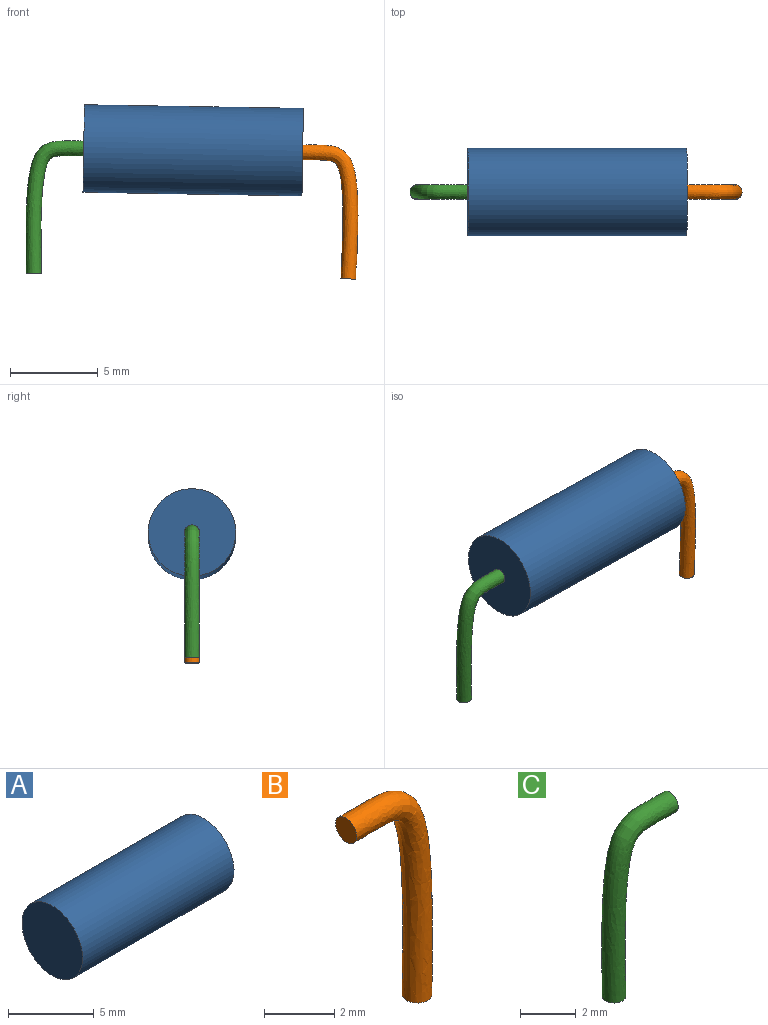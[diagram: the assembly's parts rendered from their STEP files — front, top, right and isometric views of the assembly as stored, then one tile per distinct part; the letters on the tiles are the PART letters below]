
ASSEMBLY  parts=3 mates=2
PART A: 3 faces, bbox 12.5x5x5 mm
  f0: cylinder r=2.5mm len=12.5mm, axis (-1,0,0), area 196.3mm2, adj f1,f2
  f1: plane 5x5mm, normal (1,0,0), area 19.6mm2, adj f0
  f2: plane 5x5mm, normal (-1,0,0), area 19.6mm2, adj f0
PART B: 3 faces, bbox 3.3x1.7x7.6 mm
  f0: plane 0.85x0.85mm, normal (-0.02,0,-1), area 0.6mm2, adj f2
  f1: plane 0.85x0.85mm, normal (-1,0,-0.02), area 0.6mm2, adj f2
  f2: bspline ~7.59x3.33mm, area 24.7mm2, adj f0,f1
PART C: 3 faces, bbox 3.3x1.7x7.6 mm
  f0: plane 0.85x0.85mm, normal (0.02,0,-1), area 0.6mm2, adj f2
  f1: plane 0.85x0.85mm, normal (1,0,-0.02), area 0.6mm2, adj f2
  f2: bspline ~7.59x3.33mm, area 24.7mm2, adj f0,f1
PLACE A rot(axis=(0,1,0),0.9deg) t=(-2.68,0.94,-3.08)mm
PLACE B rot(axis=(0,1,0),1.9deg) t=(-2.73,0.94,-2.97)mm
PLACE C t=(-2.64,0.94,-2.97)mm
MATE fastened A.f0 <-> B.f1  axis (1,0,-0.02) through (3.57,0.94,-3.18)mm
MATE fastened A.f0 <-> C.f1  axis (-1,0,0.02) through (-8.93,0.94,-2.97)mm
